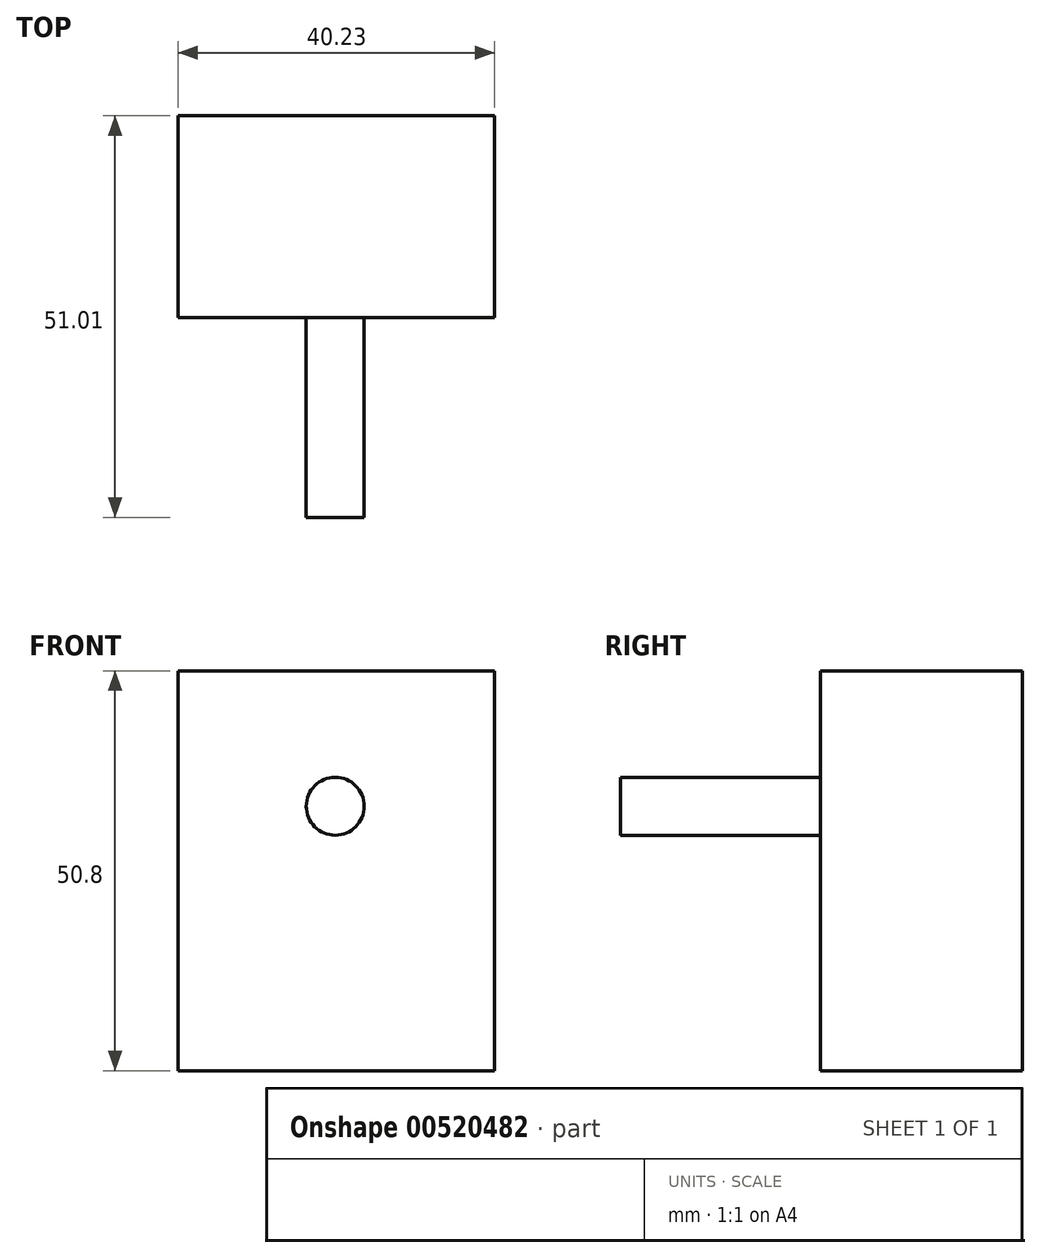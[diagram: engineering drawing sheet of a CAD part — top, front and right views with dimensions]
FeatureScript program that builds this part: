
annotation { "Feature Type Name" : "Feature", "Feature Type Description" : "" }
export const myFeature = defineFeature(function(context is Context, id is Id, definition is map)
    precondition{}
    {
        {
            var Q0;
            Q0=qCreatedBy(makeId("Top.planeOp"),FACE);
            var sketch = newSketch(context, id + "F0", { "sketchPlane" : qUnion([Q0])});
            skLineSegment(sketch, "E0.bottom", {"start": v(-15.35, 10.13) * mm, "end": v(24.88, 10.13) * mm});
            skLineSegment(sketch, "E0.top", {"start": v(-15.35, -15.48) * mm, "end": v(24.88, -15.48) * mm});
            skLineSegment(sketch, "E0.left", {"start": v(-15.35, 10.13) * mm, "end": v(-15.35, -15.48) * mm});
            skLineSegment(sketch, "E0.right", {"start": v(24.88, 10.13) * mm, "end": v(24.88, -15.48) * mm});
            skSolve(sketch);
        }
        {
            var Q0;
            Q0 = qSketchRegion(id + "F0", true);
            extrude(context, id + "F1", {"entities" : qUnion([Q0]), "depth" : 25.4 * mm, "offsetDistance" : 25.4 * mm});
        }
        {
            var Q0;
            Q0=makeQuery(id+"F1.opExtrude","CAP_FACE",FACE,{"disambiguationData":[OSD([sQuery(id+"F0.wireOp",EDGE,"E0.bottom"),sQuery(id+"F0.wireOp",EDGE,"E0.top"),sQuery(id+"F0.wireOp",EDGE,"E0.left"),sQuery(id+"F0.wireOp",EDGE,"E0.right")])],"isStart":false});
            extrude(context, id + "F2", {"entities" : qUnion([Q0]), "operationType" : NewBodyOperationType.ADD, "depth" : 25.4 * mm, "offsetDistance" : 25.4 * mm});
        }
        {
            var Q0;
            {var subQ0=sQuery(id+"F0.wireOp",EDGE,"E0.top");Q0=makeQuery(id+"F2.boolean.opBoolean","MERGE",FACE,{"derivedFrom":[makeQuery(id+"F1.opExtrude","SWEPT_FACE",FACE,{"disambiguationData":[OSD([subQ0])]}),makeQuery(id+"F2.opExtrude","SWEPT_FACE",FACE,{"disambiguationData":[OSD([subQ0])]})]});}
            var sketch = newSketch(context, id + "F3", { "sketchPlane" : qUnion([Q0])});
            skCircle(sketch, "E1", {"center": v(4.62, 33.6) * mm, "radius": 3.68 * mm});
            skSolve(sketch);
        }
        {
            var Q0;
            Q0 = qSketchRegion(id + "F3", true);
            extrude(context, id + "F4", {"entities" : qUnion([Q0]), "operationType" : NewBodyOperationType.ADD, "depth" : 25.4 * mm, "offsetDistance" : 25.4 * mm});
        }
    });
